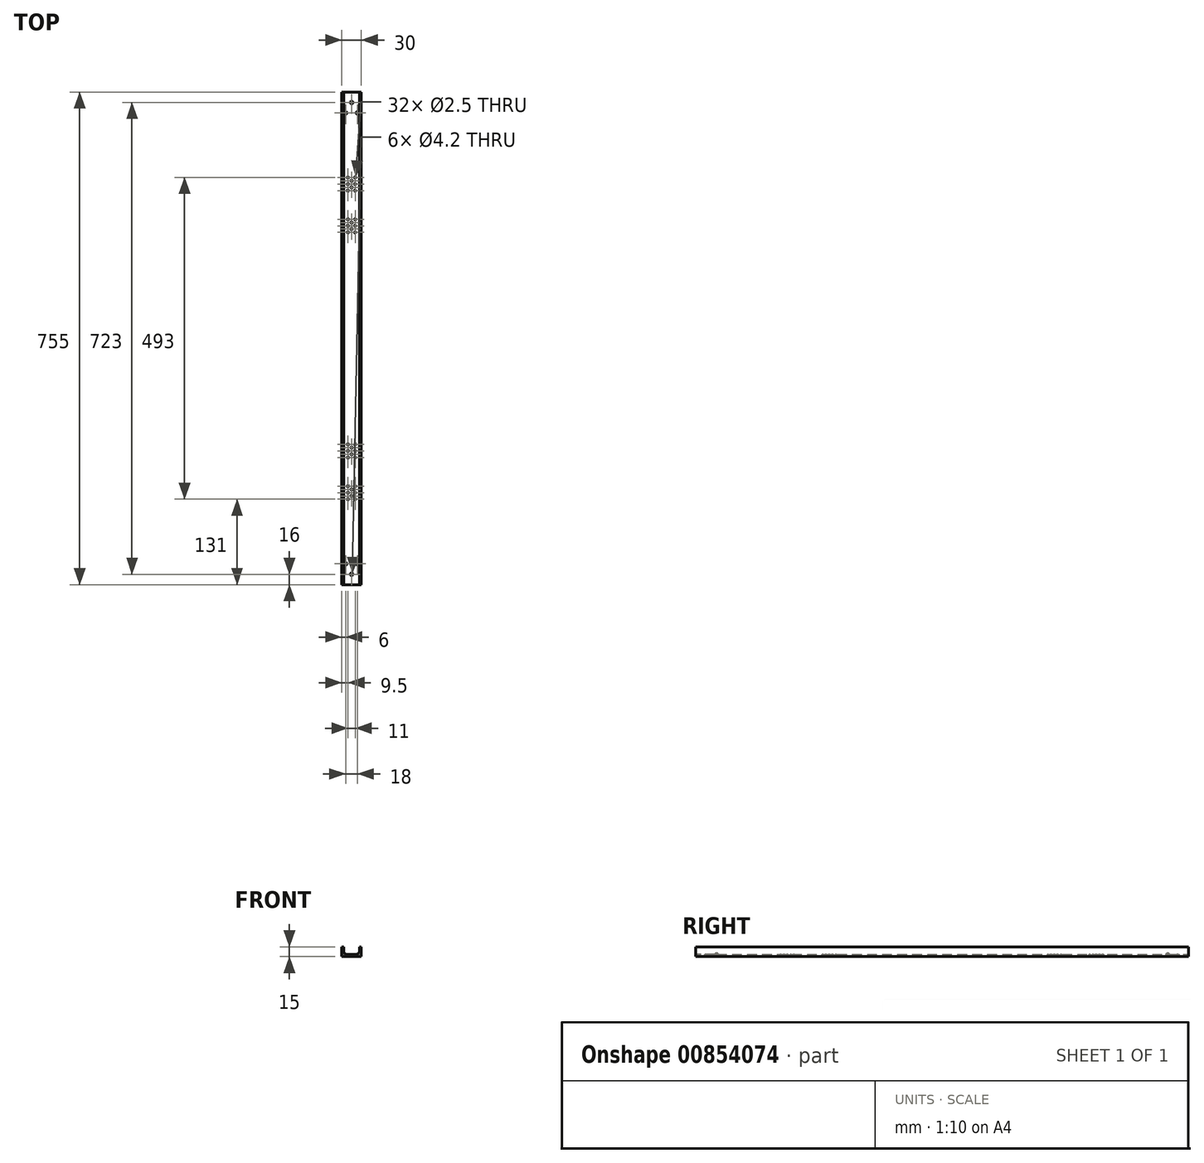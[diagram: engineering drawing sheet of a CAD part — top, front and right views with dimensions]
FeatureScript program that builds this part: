
annotation { "Feature Type Name" : "Feature", "Feature Type Description" : "" }
export const myFeature = defineFeature(function(context is Context, id is Id, definition is map)
    precondition{}
    {
        {
            var Q0;
            Q0=qCreatedBy(makeId("Front.planeOp"),FACE);
            var sketch = newSketch(context, id + "F0", { "sketchPlane" : qUnion([Q0])});
            skLineSegment(sketch, "E0", {"start": v(0, 0) * mm, "end": v(30, 0) * mm});
            skLineSegment(sketch, "E1", {"start": v(30, 0) * mm, "end": v(30, 15) * mm});
            skLineSegment(sketch, "E2", {"start": v(30, 15) * mm, "end": v(27, 15) * mm});
            skLineSegment(sketch, "E3", {"start": v(27, 15) * mm, "end": v(27, 3.5) * mm});
            skLineSegment(sketch, "E4", {"start": v(27, 3.5) * mm, "end": v(3, 3.5) * mm});
            skLineSegment(sketch, "E5", {"start": v(3, 3.5) * mm, "end": v(3, 15) * mm});
            skLineSegment(sketch, "E6", {"start": v(3, 15) * mm, "end": v(0, 15) * mm});
            skLineSegment(sketch, "E7", {"start": v(0, 15) * mm, "end": v(0, 0) * mm});
            skSolve(sketch);
        }
        {
            var Q0;
            Q0=makeQuery(id+"F0.imprint","IMPRINT",FACE,{"disambiguationData":[TD([[makeQuery(id+"F0.imprint","IMPRINT",EDGE,{"derivedFrom":sQuery(id+"F0.wireOp",EDGE,"E0")}),1.0]])]});
            extrude(context, id + "F1", {"entities" : qUnion([Q0]), "flatOperationType" : FlatOperationType.REMOVE, "thickness1" : 5 * mm, "thickness2" : 0 * mm, "thickness" : 5 * mm, "depth" : 377.5 * mm, "offsetDistance" : 25 * mm, "startOffsetBound" : StartOffsetType.BLIND, "startOffsetDistance" : 25 * mm, "domain" : OperationDomain.MODEL});
        }
        {
            var Q0;
            Q0=makeQuery(id+"F1.opExtrude","SWEPT_EDGE",EDGE,{"disambiguationData":[OSD([sQuery(id+"F0.wireOp",EDGE,"E4"),sQuery(id+"F0.wireOp",EDGE,"E5")])]});
            fillet(context, id + "F2", {"entities" : qUnion([Q0]), "radius" : 5 * mm, "tangentPropagation" : true, "allowEdgeOverflow" : false});
        }
        {
            var Q0;
            Q0=makeQuery(id+"F1.opExtrude","SWEPT_EDGE",EDGE,{"disambiguationData":[OSD([sQuery(id+"F0.wireOp",EDGE,"E3"),sQuery(id+"F0.wireOp",EDGE,"E4")])]});
            fillet(context, id + "F3", {"entities" : qUnion([Q0]), "radius" : 5 * mm, "tangentPropagation" : true, "allowEdgeOverflow" : false});
        }
        {
            var Q0;
            Q0=qCreatedBy(makeId("Top.planeOp"),FACE);
            var sketch = newSketch(context, id + "F4", { "sketchPlane" : qUnion([Q0])});
            skPoint(sketch, "E8", {"position": v(15, -16) * mm});
            skPoint(sketch, "E9", {"position": v(6, -32) * mm});
            skPoint(sketch, "E10", {"position": v(24, -32) * mm});
            skSolve(sketch);
        }
        {
            var Q0;
            Q0=sQuery(id+"F4.wireOp",VERTEX,"E10");
            var Q1;
            Q1=sQuery(id+"F4.wireOp",VERTEX,"E8");
            var Q2;
            Q2=sQuery(id+"F4.wireOp",VERTEX,"E9");
            var Q3;
            Q3=makeQuery(id+"F1.opExtrude","SWEPT_BODY",BODY,{"disambiguationData":[OSD([sQuery(id+"F0.wireOp",EDGE,"E0"),sQuery(id+"F0.wireOp",EDGE,"E1"),sQuery(id+"F0.wireOp",EDGE,"E2"),sQuery(id+"F0.wireOp",EDGE,"E3"),sQuery(id+"F0.wireOp",EDGE,"E4"),sQuery(id+"F0.wireOp",EDGE,"E5"),sQuery(id+"F0.wireOp",EDGE,"E6"),sQuery(id+"F0.wireOp",EDGE,"E7")])]});
            hole(context, id + "F5", {"style" : HoleStyle.SIMPLE, "endStyle" : HoleEndStyle.THROUGH, "oppositeDirection" : true, "standardTappedOrClearance" : lookupTablePath({ "standard" : "ISO", "engagement" : "75%", "pitch" : "0.8 mm", "size" : "M5", "type" : "Tapped" }), "standardBlindInLast" : lookupTablePath({ "standard" : "ISO", "fit" : "Normal", "engagement" : "75%", "pitch" : "0.8 mm", "size" : "M5", "type" : "Clearance & tapped" }), "holeDiameter" : 4.2 * mm, "majorDiameter" : 5 * mm, "showTappedDepth" : true, "isTappedThrough" : true, "tappedDepth" : 12 * mm, "tapClearance" : 3, "locations" : qUnion([Q0, Q1, Q2]), "scope" : qUnion([Q3]), "startStyle" : HoleStartStyle.SKETCH});
        }
        {
            var Q0;
            Q0=qCreatedBy(makeId("Top.planeOp"),FACE);
            var sketch = newSketch(context, id + "F6", { "sketchPlane" : qUnion([Q0])});
            skPoint(sketch, "E11", {"position": v(20.5, -131) * mm});
            skPoint(sketch, "E12", {"position": v(20.5, -141) * mm});
            skPoint(sketch, "E13", {"position": v(20.5, -151) * mm});
            skPoint(sketch, "E14", {"position": v(15, -136) * mm});
            skPoint(sketch, "E15", {"position": v(15, -146) * mm});
            skPoint(sketch, "E16", {"position": v(9.5, -131) * mm});
            skPoint(sketch, "E17", {"position": v(9.5, -141) * mm});
            skPoint(sketch, "E18", {"position": v(9.5, -151) * mm});
            skPoint(sketch, "E19", {"position": v(20.5, -195) * mm});
            skPoint(sketch, "E20", {"position": v(20.5, -205) * mm});
            skPoint(sketch, "E21", {"position": v(20.5, -215) * mm});
            skPoint(sketch, "E22", {"position": v(15, -200) * mm});
            skPoint(sketch, "E23", {"position": v(15, -210) * mm});
            skPoint(sketch, "E24", {"position": v(9.5, -195) * mm});
            skPoint(sketch, "E25", {"position": v(9.5, -205) * mm});
            skPoint(sketch, "E26", {"position": v(9.5, -215) * mm});
            skSolve(sketch);
        }
        {
            var Q0;
            Q0=sQuery(id+"F6.wireOp",VERTEX,"E13");
            var Q1;
            Q1=sQuery(id+"F6.wireOp",VERTEX,"E12");
            var Q2;
            Q2=sQuery(id+"F6.wireOp",VERTEX,"E11");
            var Q3;
            Q3=sQuery(id+"F6.wireOp",VERTEX,"E15");
            var Q4;
            Q4=sQuery(id+"F6.wireOp",VERTEX,"E14");
            var Q5;
            Q5=sQuery(id+"F6.wireOp",VERTEX,"E18");
            var Q6;
            Q6=sQuery(id+"F6.wireOp",VERTEX,"E17");
            var Q7;
            Q7=sQuery(id+"F6.wireOp",VERTEX,"E16");
            var Q8;
            Q8=sQuery(id+"F6.wireOp",VERTEX,"E21");
            var Q9;
            Q9=sQuery(id+"F6.wireOp",VERTEX,"E20");
            var Q10;
            Q10=sQuery(id+"F6.wireOp",VERTEX,"E19");
            var Q11;
            Q11=sQuery(id+"F6.wireOp",VERTEX,"E23");
            var Q12;
            Q12=sQuery(id+"F6.wireOp",VERTEX,"E22");
            var Q13;
            Q13=sQuery(id+"F6.wireOp",VERTEX,"E26");
            var Q14;
            Q14=sQuery(id+"F6.wireOp",VERTEX,"E25");
            var Q15;
            Q15=sQuery(id+"F6.wireOp",VERTEX,"E24");
            var Q16;
            Q16=makeQuery(id+"F1.opExtrude","SWEPT_BODY",BODY,{"disambiguationData":[OSD([sQuery(id+"F0.wireOp",EDGE,"E0"),sQuery(id+"F0.wireOp",EDGE,"E1"),sQuery(id+"F0.wireOp",EDGE,"E2"),sQuery(id+"F0.wireOp",EDGE,"E3"),sQuery(id+"F0.wireOp",EDGE,"E4"),sQuery(id+"F0.wireOp",EDGE,"E5"),sQuery(id+"F0.wireOp",EDGE,"E6"),sQuery(id+"F0.wireOp",EDGE,"E7")])]});
            hole(context, id + "F7", {"style" : HoleStyle.SIMPLE, "endStyle" : HoleEndStyle.THROUGH, "oppositeDirection" : true, "holeDiameter" : 2.5 * mm, "majorDiameter" : 3 * mm, "isTappedThrough" : true, "tappedDepth" : 12 * mm, "tapClearance" : 3, "locations" : qUnion([Q0, Q1, Q2, Q3, Q4, Q5, Q6, Q7, Q8, Q9, Q10, Q11, Q12, Q13, Q14, Q15]), "scope" : qUnion([Q16]), "startStyle" : HoleStartStyle.SKETCH});
        }
        {
            var Q0;
            Q0=makeQuery(id+"F1.opExtrude","SWEPT_BODY",BODY,{"disambiguationData":[OSD([sQuery(id+"F0.wireOp",EDGE,"E0"),sQuery(id+"F0.wireOp",EDGE,"E1"),sQuery(id+"F0.wireOp",EDGE,"E2"),sQuery(id+"F0.wireOp",EDGE,"E3"),sQuery(id+"F0.wireOp",EDGE,"E4"),sQuery(id+"F0.wireOp",EDGE,"E5"),sQuery(id+"F0.wireOp",EDGE,"E6"),sQuery(id+"F0.wireOp",EDGE,"E7")])]});
            var Q1;
            Q1=makeQuery(id+"F1.opExtrude","CAP_FACE",FACE,{"disambiguationData":[OSD([sQuery(id+"F0.wireOp",EDGE,"E0"),sQuery(id+"F0.wireOp",EDGE,"E1"),sQuery(id+"F0.wireOp",EDGE,"E2"),sQuery(id+"F0.wireOp",EDGE,"E3"),sQuery(id+"F0.wireOp",EDGE,"E4"),sQuery(id+"F0.wireOp",EDGE,"E5"),sQuery(id+"F0.wireOp",EDGE,"E6"),sQuery(id+"F0.wireOp",EDGE,"E7")])],"isStart":false});
            mirror(context, id + "F8", {"operationType" : NewBodyOperationType.ADD, "entities" : qUnion([Q0]), "mirrorPlane" : qUnion([Q1])});
        }
    });
